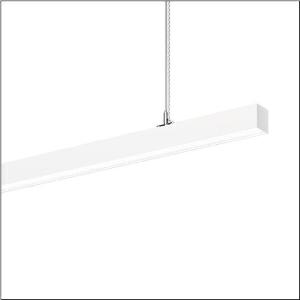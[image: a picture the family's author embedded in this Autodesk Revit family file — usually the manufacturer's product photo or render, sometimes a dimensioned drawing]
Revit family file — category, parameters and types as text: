
# Revit family: silica_r__21_51mx30tbt5w_3ed0
name_source: partatom
category: Lighting Fixtures
units: mm (PartAtom-declared; Revit-internal decimal feet)

## family parameters
Cut with Voids When Loaded = No
Host = Face
Light Source = No
Part Type = Normal
Room Calculation Point = No
Round Connector Dimension = Use Diameter
Shared = No

## types (1)
- --- (1 x LED, 5150 lm, 42.2 W, 6500K)
    Apparent Load = 42 VA
    CIE Flux Codes = 47 79 96 58 100
    Color Rendering = 80
    Color Temperature = 6500K
    Default Elevation = 1800 mm
    Description = Silica® 21, office luminaire, primary optical cover: cover, of PMMA, opal, light emission: direct/indirect distribution, primary light characteristic: symmetric, installation type: suspended mounting, LED, rated luminous flux: 5.150lm, luminous efficacy: 116lm/W, light colour: 8tw, colour temperature: 2700..6500K, control gear: ECG DALI, with terminal, 3+2-pole, max. 2.5mm², mains connection: 220..240V, AC, 50/60Hz, rated input power: 44.3W, luminaire housing, of aluminium, traffic white (RAL 9016), length: 1.504mm, width: 53mm, height: 53mm, protection rating (complete): IP20, insulation class (complete): insulation class I (protective earthing), certification: CE, permissible operating ambient temperature: 0..+35°C, standard: EN 50419, packaging unit: 1 piece
    Height = 53 mm
    Lamp = 1 x LED
    Lamp Light Flux = 5150 lm
    Lamp Power = 42.2 W
    Lamp count = 1
    Length = 1504 mm
    Luminous efficacy = 122 lm/W
    Manufacturer = Siteco
    ModVariant = No
    Model = 51MX30TBT5W
    Mounting Place = Ceiling
    Mounting Type = Pendant
    Number of Poles = 1
    OnlyDefault = Yes
    Power Factor = 1
    Product Name = Silica® 21
    Product group = office luminaire | ceiling pendant
    ProductGroupID = 902
    Protection Class = Protection class I
    Protection Degree = IP 20
    RLX_Detail_Level = 1
    RLX_Emergency_Light_Flux = 0 lm
    RLX_Emergency_Type = 0
    RLX_Emergency_Type_DB = No
    RlxData = <blob elided: 18165 chars, md5=fa4d56a1>
    Socket = socket
    Standby Power = 0 W
    System Light Flux = 5150 lm
    System Power = 42 W
    Type Comments = individual setting
    Type Image = l_1335916.jpg
    URL = http://relux.com
    VarID = @adj_109453
    Voltage = 0 V
    Weight = 0.00 kg
    Width = 53 mm

## geometry (parser evidence)
native form markers: Blend x4, Sweep x15
no freeform markers — native parametric forms only
